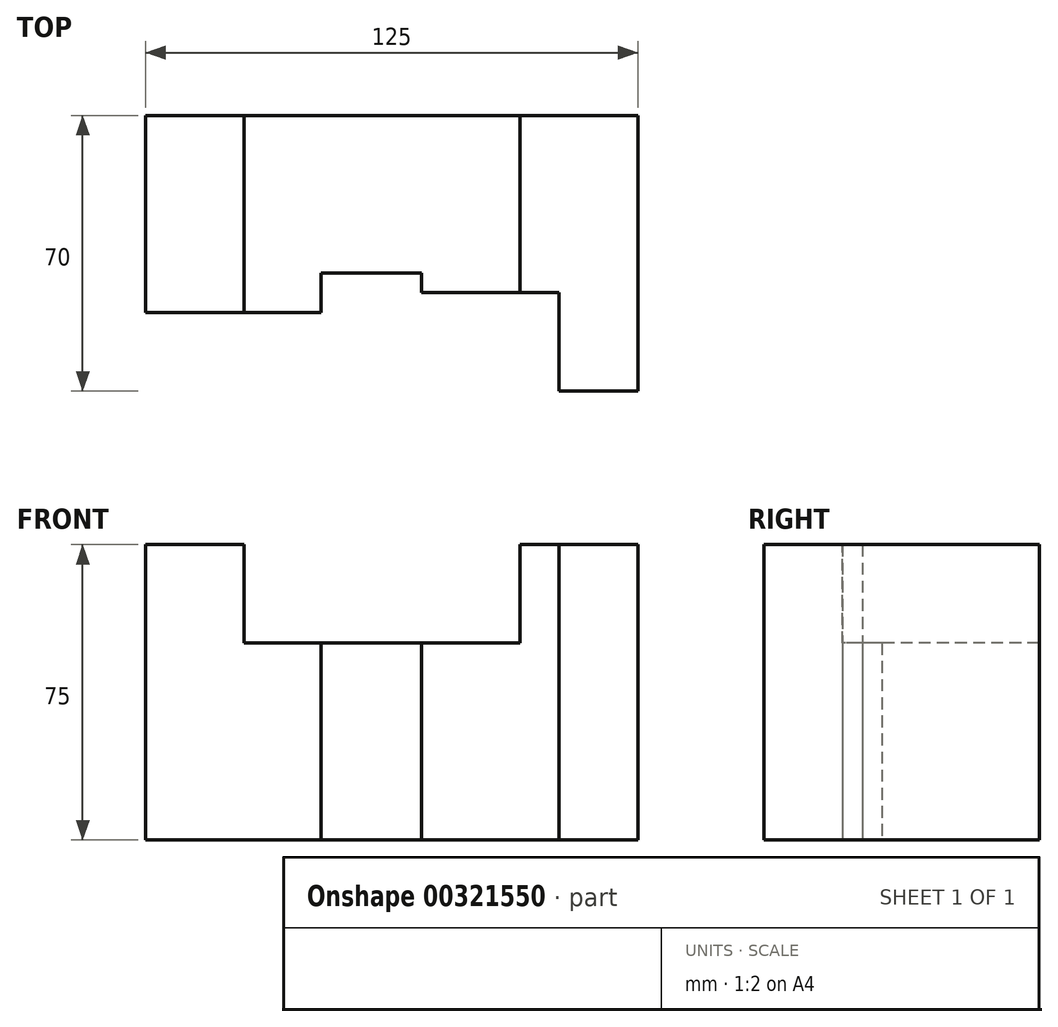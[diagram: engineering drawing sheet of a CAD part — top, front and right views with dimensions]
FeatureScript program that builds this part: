
annotation { "Feature Type Name" : "Feature", "Feature Type Description" : "" }
export const myFeature = defineFeature(function(context is Context, id is Id, definition is map)
    precondition{}
    {
        {
            var Q0;
            Q0=qCreatedBy(makeId("Right.planeOp"),FACE);
            var sketch = newSketch(context, id + "F0", { "sketchPlane" : qUnion([Q0])});
            skLineSegment(sketch, "E0.bottom", {"start": v(0, 0) * mm, "end": v(70, 0) * mm});
            skLineSegment(sketch, "E0.top", {"start": v(0, 75) * mm, "end": v(70, 75) * mm});
            skLineSegment(sketch, "E0.left", {"start": v(0, 0) * mm, "end": v(0, 75) * mm});
            skLineSegment(sketch, "E0.right", {"start": v(70, 0) * mm, "end": v(70, 75) * mm});
            skSolve(sketch);
        }
        {
            var Q0;
            Q0=makeQuery(id+"F0.imprint","IMPRINT",FACE,{"disambiguationData":[TD([[makeQuery(id+"F0.imprint","IMPRINT",EDGE,{"derivedFrom":sQuery(id+"F0.wireOp",EDGE,"E0.bottom")}),1.0]])]});
            extrude(context, id + "F1", {"entities" : qUnion([Q0]), "depth" : 125 * mm});
        }
        {
            var Q0;
            Q0=makeQuery(id+"F1.opExtrude","CAP_FACE",FACE,{"disambiguationData":[OSD([sQuery(id+"F0.wireOp",EDGE,"E0.bottom"),sQuery(id+"F0.wireOp",EDGE,"E0.top"),sQuery(id+"F0.wireOp",EDGE,"E0.left"),sQuery(id+"F0.wireOp",EDGE,"E0.right")])],"isStart":false});
            var sketch = newSketch(context, id + "F2", { "sketchPlane" : qUnion([Q0])});
            skLineSegment(sketch, "E1.bottom", {"start": v(0, 75) * mm, "end": v(20, 75) * mm});
            skLineSegment(sketch, "E1.top", {"start": v(0, 0) * mm, "end": v(20, 0) * mm});
            skLineSegment(sketch, "E1.left", {"start": v(0, 75) * mm, "end": v(0, 0) * mm});
            skLineSegment(sketch, "E1.right", {"start": v(20, 75) * mm, "end": v(20, 0) * mm});
            skSolve(sketch);
        }
        {
            var Q0;
            Q0=makeQuery(id+"F2.imprint","IMPRINT",FACE,{"disambiguationData":[TD([[makeQuery(id+"F2.imprint","IMPRINT",EDGE,{"derivedFrom":sQuery(id+"F2.wireOp",EDGE,"E1.bottom")}),-1.0]])]});
            extrude(context, id + "F3", {"entities" : qUnion([Q0]), "operationType" : NewBodyOperationType.REMOVE, "endBound" : BoundingType.THROUGH_ALL, "oppositeDirection" : true, "depth" : 25 * mm, "hasSecondDirection" : true, "secondDirectionOppositeDirection" : true, "secondDirectionDepth" : 20 * mm});
        }
        {
            var Q0;
            {var subQ0=sQuery(id+"F2.wireOp",EDGE,"E1.right");Q0=makeQuery(id+"F2.imprint","IMPRINT",FACE,{"disambiguationData":[TD([[makeQuery(id+"F2.imprint","IMPRINT",EDGE,{"derivedFrom":subQ0}),1.0]])]});}
            var sketch = newSketch(context, id + "F4", { "sketchPlane" : qUnion([Q0])});
            skLineSegment(sketch, "E2.bottom", {"start": v(20, 75) * mm, "end": v(30, 75) * mm});
            skLineSegment(sketch, "E2.top", {"start": v(20, 0) * mm, "end": v(30, 0) * mm});
            skLineSegment(sketch, "E2.left", {"start": v(20, 75) * mm, "end": v(20, 0) * mm});
            skLineSegment(sketch, "E2.right", {"start": v(30, 75) * mm, "end": v(30, 0) * mm});
            skSolve(sketch);
        }
        {
            var Q0;
            Q0=makeQuery(id+"F4.imprint","IMPRINT",FACE,{"disambiguationData":[TD([[makeQuery(id+"F4.imprint","IMPRINT",EDGE,{"derivedFrom":sQuery(id+"F4.wireOp",EDGE,"E2.bottom")}),-1.0]])]});
            extrude(context, id + "F5", {"entities" : qUnion([Q0]), "operationType" : NewBodyOperationType.REMOVE, "oppositeDirection" : true, "depth" : 80.5 * mm, "hasSecondDirection" : true, "secondDirectionOppositeDirection" : true, "secondDirectionDepth" : 55 * mm});
        }
        {
            var Q0;
            Q0=makeQuery(id+"F1.opExtrude","CAP_FACE",FACE,{"disambiguationData":[OSD([sQuery(id+"F0.wireOp",EDGE,"E0.bottom"),sQuery(id+"F0.wireOp",EDGE,"E0.top"),sQuery(id+"F0.wireOp",EDGE,"E0.left"),sQuery(id+"F0.wireOp",EDGE,"E0.right")])],"isStart":false});
            var sketch = newSketch(context, id + "F6", { "sketchPlane" : qUnion([Q0])});
            skLineSegment(sketch, "E3.bottom", {"start": v(70, 75) * mm, "end": v(0, 75) * mm});
            skLineSegment(sketch, "E3.top", {"start": v(70, 50) * mm, "end": v(0, 50) * mm});
            skLineSegment(sketch, "E3.left", {"start": v(70, 75) * mm, "end": v(70, 50) * mm});
            skLineSegment(sketch, "E3.right", {"start": v(0, 75) * mm, "end": v(0, 50) * mm});
            skSolve(sketch);
        }
        {
            var Q0;
            Q0=makeQuery(id+"F6.imprint","IMPRINT",FACE,{"disambiguationData":[TD([[makeQuery(id+"F6.imprint","IMPRINT",EDGE,{"derivedFrom":sQuery(id+"F6.wireOp",EDGE,"E3.bottom")}),-1.0]])]});
            extrude(context, id + "F7", {"entities" : qUnion([Q0]), "operationType" : NewBodyOperationType.REMOVE, "oppositeDirection" : true, "depth" : 100 * mm, "hasSecondDirection" : true, "secondDirectionOppositeDirection" : true, "secondDirectionDepth" : 30 * mm});
        }
        {
            var Q0;
            Q0=makeQuery(id+"F4.imprint","IMPRINT",FACE,{"disambiguationData":[TD([[makeQuery(id+"F4.imprint","IMPRINT",EDGE,{"derivedFrom":sQuery(id+"F4.wireOp",EDGE,"E2.bottom")}),-1.0]])]});
            var sketch = newSketch(context, id + "F8", { "sketchPlane" : qUnion([Q0])});
            skLineSegment(sketch, "E4.bottom", {"start": v(30, 75) * mm, "end": v(25, 75) * mm});
            skLineSegment(sketch, "E4.top", {"start": v(30, 0) * mm, "end": v(25, 0) * mm});
            skLineSegment(sketch, "E4.left", {"start": v(30, 75) * mm, "end": v(30, 0) * mm});
            skLineSegment(sketch, "E4.right", {"start": v(25, 75) * mm, "end": v(25, 0) * mm});
            skSolve(sketch);
        }
        {
            var Q0;
            {var subQ0=sQuery(id+"F8.wireOp",EDGE,"E4.right");Q0=makeQuery(id+"F8.imprint","IMPRINT",FACE,{"disambiguationData":[TD([[makeQuery(id+"F8.imprint","IMPRINT",EDGE,{"derivedFrom":subQ0}),-1.0]])]});}
            extrude(context, id + "F9", {"entities" : qUnion([Q0]), "operationType" : NewBodyOperationType.REMOVE, "oppositeDirection" : true, "depth" : 80.5 * mm, "hasSecondDirection" : true, "secondDirectionOppositeDirection" : true, "secondDirectionDepth" : 20 * mm});
        }
    });
